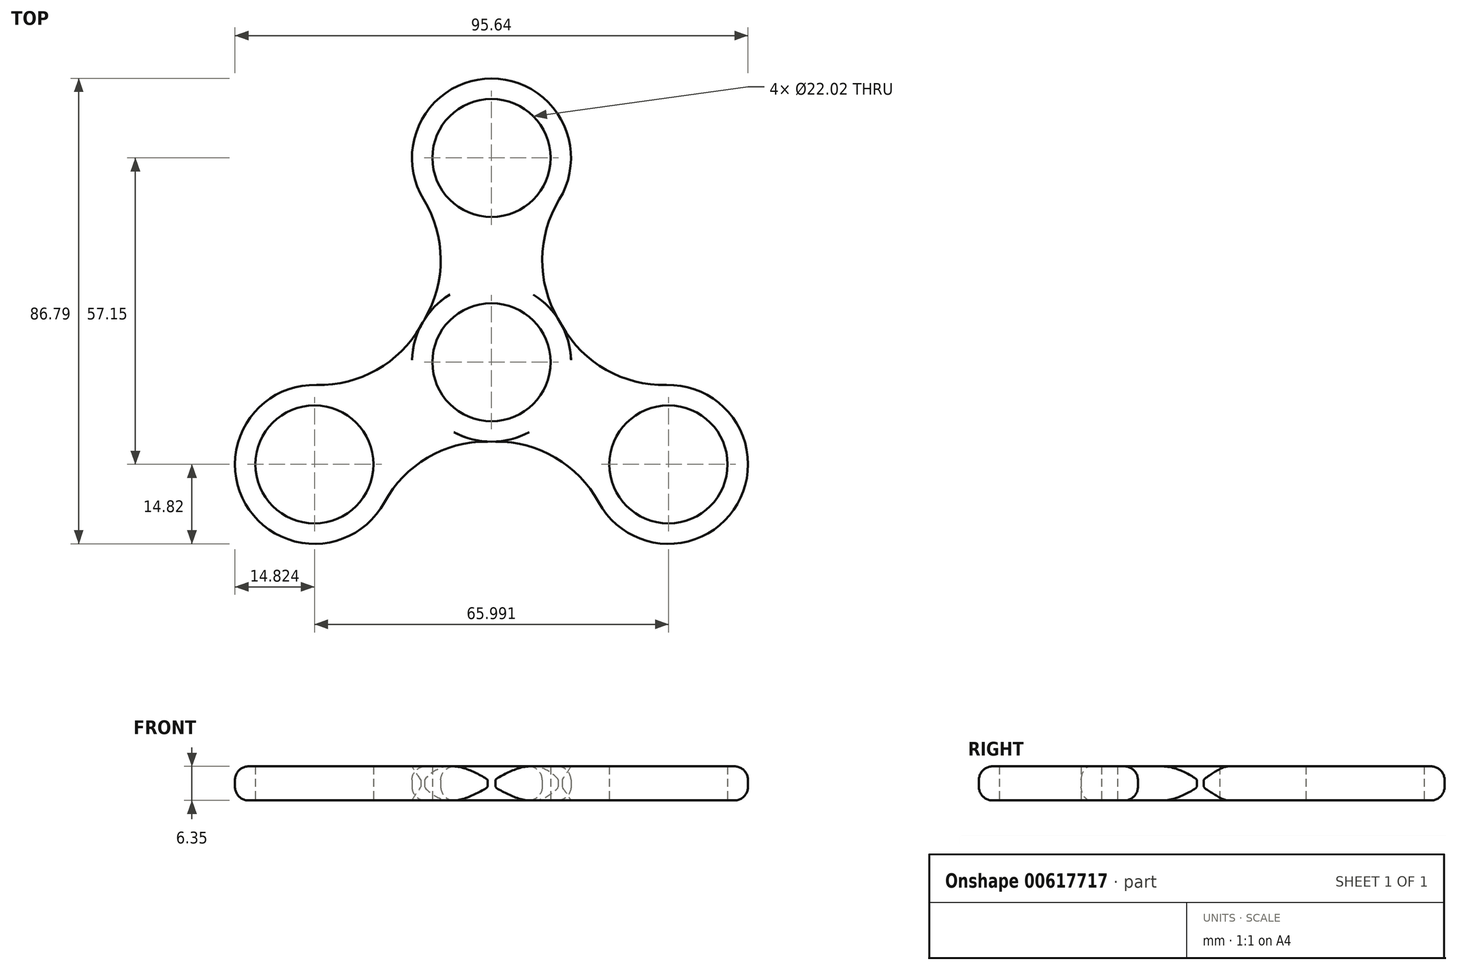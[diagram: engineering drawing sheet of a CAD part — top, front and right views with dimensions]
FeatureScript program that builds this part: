
annotation { "Feature Type Name" : "Feature", "Feature Type Description" : "" }
export const myFeature = defineFeature(function(context is Context, id is Id, definition is map)
    precondition{}
    {
        {
            var Q0;
            Q0=qCreatedBy(makeId("Top.planeOp"),FACE);
            var sketch = newSketch(context, id + "F0", { "sketchPlane" : qUnion([Q0])});
            skCircle(sketch, "E0", {"center": v(0, 0) * mm, "radius": 11.01 * mm});
            skLineSegment(sketch, "E1", {"start": v(0, 0) * mm, "end": v(0, 38.1) * mm});
            skLineSegment(sketch, "E2", {"start": v(0, 0) * mm, "end": v(33, -19.05) * mm});
            skLineSegment(sketch, "E3", {"start": v(0, 0) * mm, "end": v(-33, -19.05) * mm});
            skCircle(sketch, "E4", {"center": v(0, 38.1) * mm, "radius": 11.01 * mm});
            skCircle(sketch, "E5", {"center": v(-33, -19.05) * mm, "radius": 11.01 * mm});
            skCircle(sketch, "E6", {"center": v(33, -19.05) * mm, "radius": 11.01 * mm});
            skCircle(sketch, "E7", {"center": v(0, 0) * mm, "radius": 14.82 * mm});
            skCircle(sketch, "E8", {"center": v(33, -19.05) * mm, "radius": 14.82 * mm});
            skCircle(sketch, "E9", {"center": v(-33, -19.05) * mm, "radius": 14.82 * mm});
            skCircle(sketch, "E10", {"center": v(0, 38.1) * mm, "radius": 14.82 * mm});
            skArc(sketch, "E11", {"start": v(-32.62, -4.23) * mm, "mid": v(-21.06, -1.24) * mm, "end": v(-12.84, 7.41) * mm});
            skArc(sketch, "E12", {"start": v(0, -14.82) * mm, "mid": v(-11.6, -17.62) * mm, "end": v(-19.98, -26.13) * mm});
            skArc(sketch, "E13", {"start": v(19.98, -26.13) * mm, "mid": v(11.6, -17.62) * mm, "end": v(0, -14.82) * mm});
            skArc(sketch, "E14", {"start": v(12.84, 7.41) * mm, "mid": v(21.06, -1.24) * mm, "end": v(32.62, -4.23) * mm});
            skArc(sketch, "E15", {"start": v(-12.84, 7.41) * mm, "mid": v(-9.45, 18.86) * mm, "end": v(-12.64, 30.37) * mm});
            skArc(sketch, "E16", {"start": v(12.64, 30.37) * mm, "mid": v(9.45, 18.86) * mm, "end": v(12.84, 7.41) * mm});
            skSolve(sketch);
        }
        {
            var Q0;
            Q0 = qSketchRegion(id + "F0", true);
            extrude(context, id + "F1", {"entities" : qUnion([Q0]), "depth" : 6.35 * mm, "offsetDistance" : 25.4 * mm});
        }
        {
            var Q0;
            Q0=makeQuery(id+"F1.opExtrude","CAP_EDGE",EDGE,{"disambiguationData":[OSD([sQuery(id+"F0.wireOp",EDGE,"E15")])],"isStart":false});
            var Q1;
            Q1=makeQuery(id+"F1.opExtrude","CAP_EDGE",EDGE,{"disambiguationData":[OSD([sQuery(id+"F0.wireOp",EDGE,"E11")])],"isStart":false});
            var Q2;
            Q2=makeQuery(id+"F1.opExtrude","CAP_EDGE",EDGE,{"disambiguationData":[OSD([sQuery(id+"F0.wireOp",EDGE,"E14")])],"isStart":false});
            fillet(context, id + "F2", {"entities" : qUnion([Q0, Q1, Q2]), "radius" : 2.54 * mm, "tangentPropagation" : true, "allowEdgeOverflow" : false});
        }
        {
            var Q0;
            Q0=makeQuery(id+"F1.opExtrude","CAP_EDGE",EDGE,{"disambiguationData":[OSD([sQuery(id+"F0.wireOp",EDGE,"E12")])],"isStart":true});
            var Q1;
            Q1=makeQuery(id+"F1.opExtrude","CAP_EDGE",EDGE,{"disambiguationData":[OSD([sQuery(id+"F0.wireOp",EDGE,"E13")])],"isStart":true});
            var Q2;
            Q2=makeQuery(id+"F1.opExtrude","CAP_EDGE",EDGE,{"disambiguationData":[OSD([sQuery(id+"F0.wireOp",EDGE,"E14")])],"isStart":true});
            var Q3;
            Q3=makeQuery(id+"F1.opExtrude","CAP_EDGE",EDGE,{"disambiguationData":[OSD([sQuery(id+"F0.wireOp",EDGE,"E16")])],"isStart":true});
            var Q4;
            Q4=makeQuery(id+"F1.opExtrude","CAP_EDGE",EDGE,{"disambiguationData":[OSD([sQuery(id+"F0.wireOp",EDGE,"E15")])],"isStart":true});
            fillet(context, id + "F3", {"entities" : qUnion([Q0, Q1, Q2, Q3, Q4]), "radius" : 2.54 * mm, "tangentPropagation" : true, "allowEdgeOverflow" : false});
        }
    });
